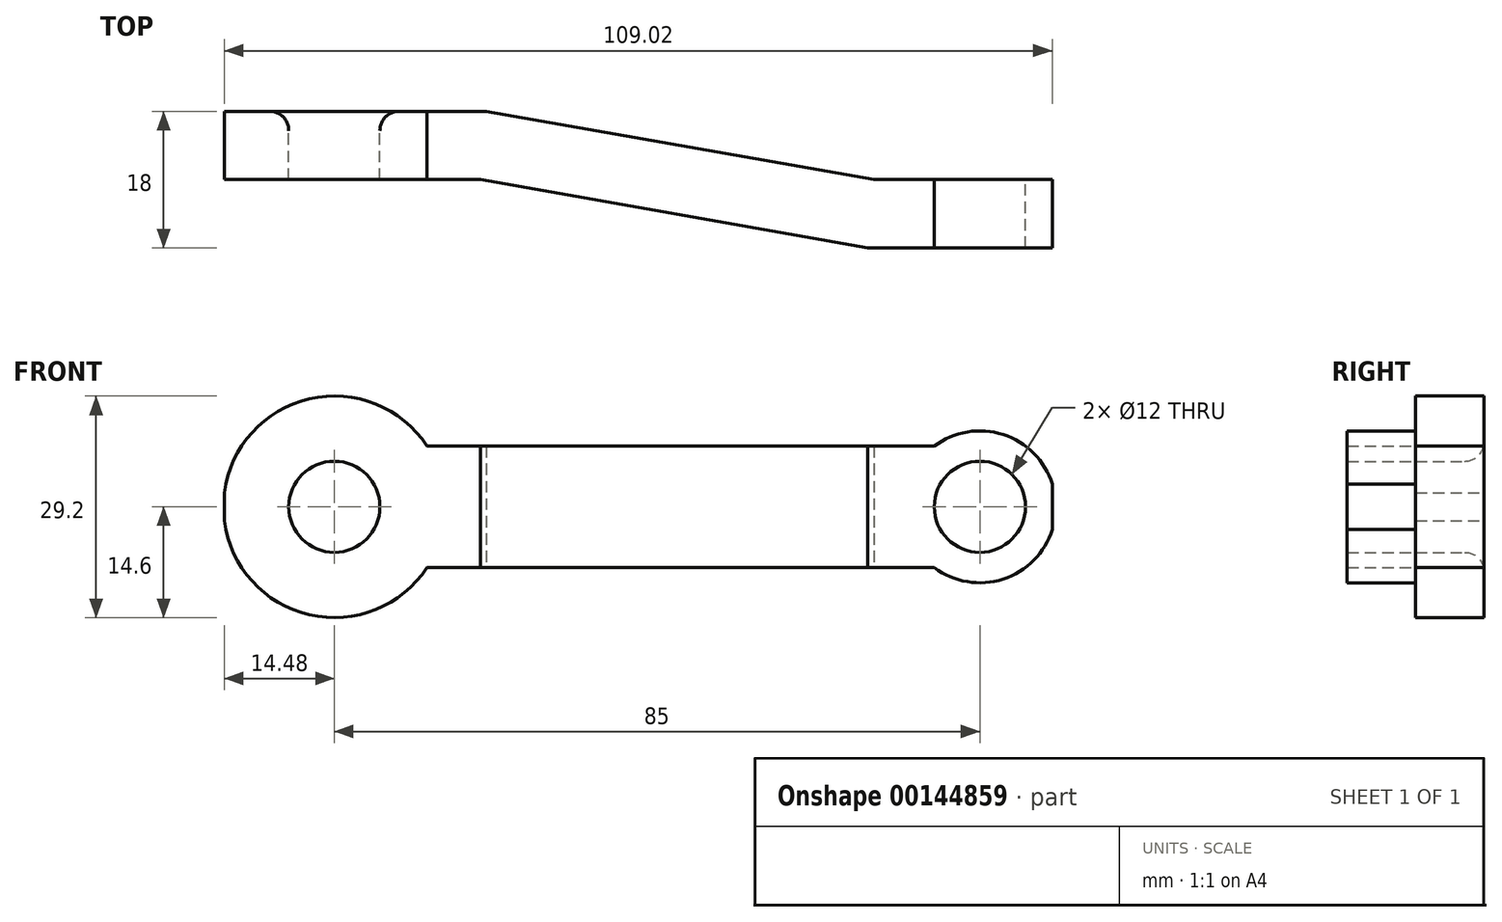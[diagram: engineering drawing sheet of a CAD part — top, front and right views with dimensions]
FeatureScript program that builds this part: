
annotation { "Feature Type Name" : "Feature", "Feature Type Description" : "" }
export const myFeature = defineFeature(function(context is Context, id is Id, definition is map)
    precondition{}
    {
        {
            var Q0;
            Q0=qCreatedBy(makeId("Front.planeOp"),FACE);
            var sketch = newSketch(context, id + "F0", { "sketchPlane" : qUnion([Q0])});
            skCircle(sketch, "E0", {"center": v(0, 0) * mm, "radius": 14.6 * mm});
            skCircle(sketch, "E1", {"center": v(85, 0) * mm, "radius": 10 * mm});
            skLineSegment(sketch, "E2", {"start": v(0, 0) * mm, "end": v(85, 0) * mm, "construction": true});
            skCircle(sketch, "E3", {"center": v(0, 0) * mm, "radius": 6 * mm});
            skCircle(sketch, "E4", {"center": v(85, 0) * mm, "radius": 6 * mm});
            skLineSegment(sketch, "E5", {"start": v(12.2, 8) * mm, "end": v(79, 8) * mm});
            skLineSegment(sketch, "E6.MirrorCS", {"start": v(12.2, -8) * mm, "end": v(79, -8) * mm});
            skSolve(sketch);
        }
        {
            var Q0;
            Q0 = qSketchRegion(id + "F0", true);
            extrude(context, id + "F1", {"entities" : qUnion([Q0]), "depth" : 25 * mm});
        }
        {
            var Q0;
            Q0=qCreatedBy(makeId("Top.planeOp"),FACE);
            var sketch = newSketch(context, id + "F2", { "sketchPlane" : qUnion([Q0])});
            skLineSegment(sketch, "E7", {"start": v(-14.48, 0) * mm, "end": v(20, 0) * mm});
            skLineSegment(sketch, "E8", {"start": v(20, 0) * mm, "end": v(71.04, -9) * mm});
            skLineSegment(sketch, "E9", {"start": v(71.04, -9) * mm, "end": v(94.54, -9) * mm});
            skLineSegment(sketch, "E10.0", {"start": v(70.25, -18) * mm, "end": v(94.54, -18) * mm});
            skLineSegment(sketch, "E10.1", {"start": v(19.21, -9) * mm, "end": v(70.25, -18) * mm});
            skLineSegment(sketch, "E10.2", {"start": v(-14.48, -9) * mm, "end": v(19.21, -9) * mm});
            skLineSegment(sketch, "E11", {"start": v(94.54, -9) * mm, "end": v(94.54, -18) * mm});
            skLineSegment(sketch, "E12", {"start": v(-14.48, 0) * mm, "end": v(-14.48, -9) * mm});
            skLineSegment(sketch, "E13", {"start": v(95, 0) * mm, "end": v(95, -25) * mm});
            skLineSegment(sketch, "E14", {"start": v(-14.6, -25) * mm, "end": v(-14.6, 0) * mm});
            skSolve(sketch);
        }
        {
            var Q0;
            Q0 = qSketchRegion(id + "F2", true);
            extrude(context, id + "F3", {"entities" : qUnion([Q0]), "operationType" : NewBodyOperationType.INTERSECT, "endBound" : BoundingType.SYMMETRIC, "depth" : 635 * mm});
        }
        {
            var Q0;
            Q0=makeQuery(id+"F3.boolean.opBoolean","INTERSECT",EDGE,{"derivedFrom":[makeQuery(id+"F1.opExtrude","SWEPT_FACE",FACE,{"disambiguationData":[OSD([sQuery(id+"F0.wireOp",EDGE,"E3")])]}),makeQuery(id+"F3.boolean.toolComplement.opBoolean","COPY",FACE,{"derivedFrom":makeQuery(id+"F3.opExtrude","SWEPT_FACE",FACE,{"disambiguationData":[OSD([sQuery(id+"F2.wireOp",EDGE,"E10.2")])]})})]});
            var Q1;
            Q1=makeQuery(id+"F3.boolean.opBoolean","INTERSECT",EDGE,{"derivedFrom":[makeQuery(id+"F1.opExtrude","SWEPT_FACE",FACE,{"disambiguationData":[OSD([sQuery(id+"F0.wireOp",EDGE,"E4")])]}),makeQuery(id+"F3.boolean.toolComplement.opBoolean","COPY",FACE,{"derivedFrom":makeQuery(id+"F3.opExtrude","SWEPT_FACE",FACE,{"disambiguationData":[OSD([sQuery(id+"F2.wireOp",EDGE,"E10.0")])]})})]});
            var Q2;
            Q2=makeQuery(id+"F1.opExtrude","CAP_EDGE",EDGE,{"disambiguationData":[OSD([sQuery(id+"F0.wireOp",EDGE,"E3")])],"isStart":true});
            var Q3;
            Q3=makeQuery(id+"F3.boolean.opBoolean","INTERSECT",EDGE,{"derivedFrom":[makeQuery(id+"F1.opExtrude","SWEPT_FACE",FACE,{"disambiguationData":[OSD([sQuery(id+"F0.wireOp",EDGE,"E4")])]}),makeQuery(id+"F3.boolean.toolComplement.opBoolean","COPY",FACE,{"derivedFrom":makeQuery(id+"F3.opExtrude","SWEPT_FACE",FACE,{"disambiguationData":[OSD([sQuery(id+"F2.wireOp",EDGE,"E9")])]})})]});
            fillet(context, id + "F4", {"entities" : qUnion([Q0, Q1, Q2, Q3]), "radius" : 2.54 * mm, "tangentPropagation" : true, "allowEdgeOverflow" : false});
        }
    });
